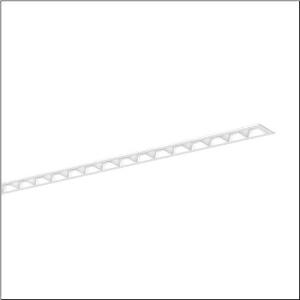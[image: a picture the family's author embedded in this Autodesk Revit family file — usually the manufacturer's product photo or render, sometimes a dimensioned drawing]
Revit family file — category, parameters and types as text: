
# Revit family: silica_r__21_51mx16dc4awb_037f
name_source: partatom
category: Lighting Fixtures
units: mm (PartAtom-declared; Revit-internal decimal feet)

## family parameters
Cut with Voids When Loaded = No
Host = Face
Light Source = No
Part Type = Normal
Room Calculation Point = No
Round Connector Dimension = Use Diameter
Shared = No

## types (1)
- --- (1 x LED, 10800 lm, 60.6 W, 4000K)
    Apparent Load = 61 VA
    CIE Flux Codes = 83 98 100 100 100
    Color Rendering = 80
    Color Temperature = 4000K
    Default Elevation = 1800 mm
    Description = Silica® 21, office luminaire, primary light control with darklight reflector, of PMMA, white, CAT 2 (L<= 3000cd/m²), light emission: direct distribution, primary light characteristic: symmetric, installation type: recessed, LED, rated luminous flux: 10.800lm, luminous efficacy: 178lm/W, light colour: 840, colour temperature: 4000K, with terminal, 3+2-pole, max. 2.5mm², mains connection: 220..240V, AC, 50/60Hz, rated input power: 60.6W, luminaire housing, of aluminium, traffic white (RAL 9016), length: 3.028mm, width: 79mm, height: 53mm, protection rating (complete): IP20, insulation class (complete): insulation class I (protective earthing), certification: CE, permissible operating ambient temperature: 0..+35°C, standard: EN 50419, packaging unit: 1 piece
    Height = 0 mm  [stored 0 ft]
    Lamp = 1 x LED
    Lamp Light Flux = 10800 lm
    Lamp Power = 60.6 W
    Lamp count = 1
    Length = 3027 mm
    Luminous efficacy = 178 lm/W
    Manufacturer = Siteco
    ModVariant = No
    Model = 51MX16DC4AWB
    Mounting Place = Ceiling
    Mounting Type = Recessed
    Number of Poles = 1
    OnlyDefault = Yes
    Power Factor = 1
    Product Name = Silica® 21
    Product group = office luminaire | ceiling recessed
    ProductGroupID = 400
    Protection Class = Protection class I
    Protection Degree = IP 20
    RLX_Detail_Level = 1
    RLX_Emergency_Light_Flux = 0 lm
    RLX_Emergency_Type = 0
    RLX_Emergency_Type_DB = No
    RlxData = <blob elided: 61049 chars, md5=045489d2>
    Socket = socket
    Standby Power = 0 W
    System Light Flux = 10800 lm
    System Power = 61 W
    Type Comments = factory setting: luminous flux: 100 % | dim-lin: 254 | 336 mA
    Type Image = l_1335884.jpg
    URL = http://relux.com
    VarID = @adj_093881
    Voltage = 0 V
    Weight = 0.00 kg
    Width = 79 mm

note: [stored X ft] marks values corroborated as IEEE doubles in the binary element streams (Revit-internal decimal feet)

## geometry (parser evidence)
native form markers: Blend x4, Sweep x11
no freeform markers — native parametric forms only
